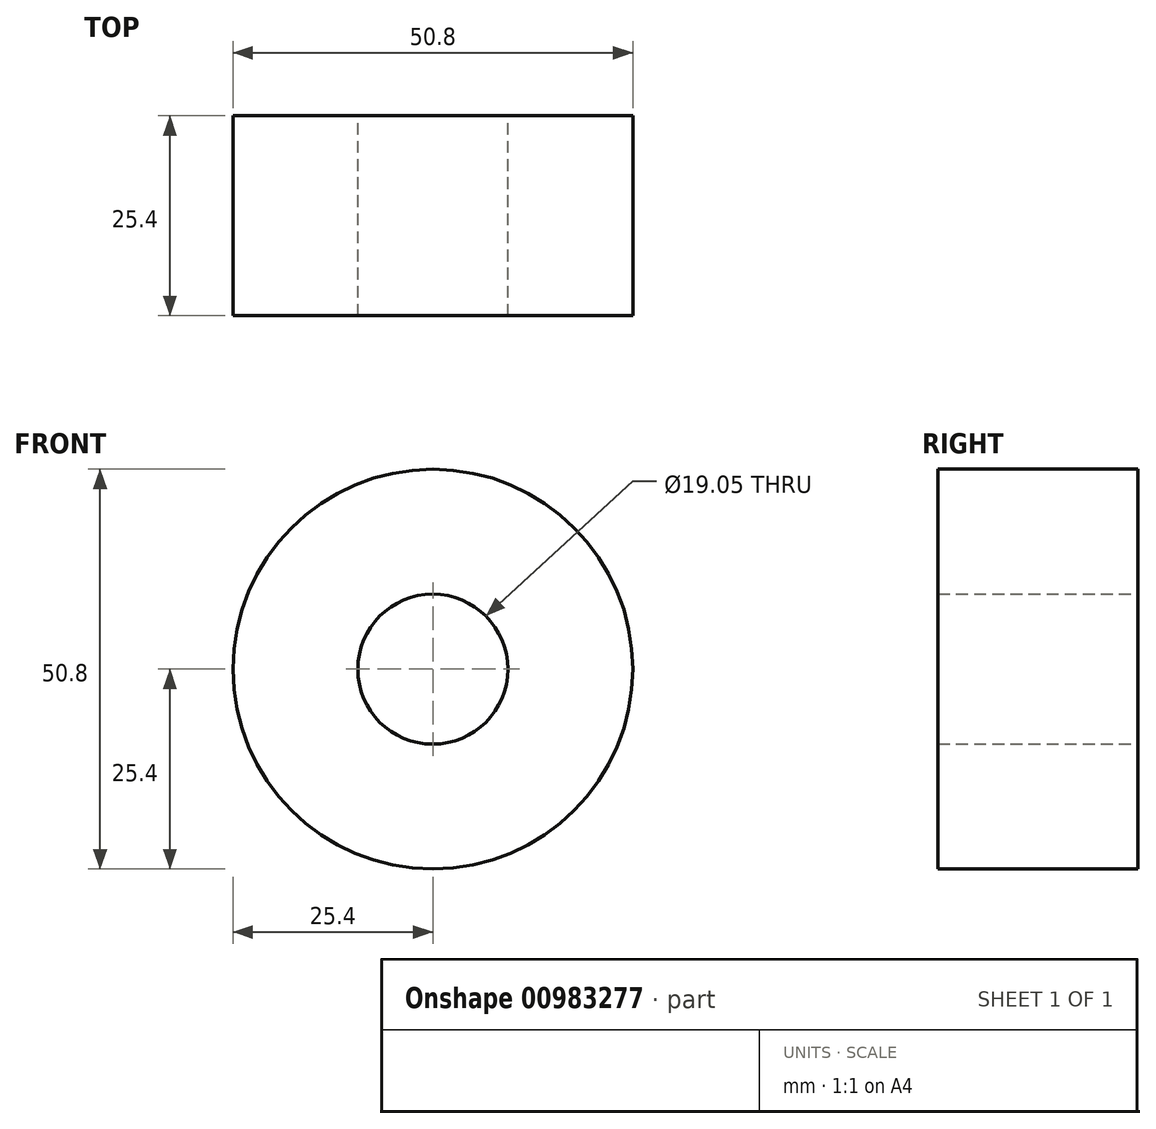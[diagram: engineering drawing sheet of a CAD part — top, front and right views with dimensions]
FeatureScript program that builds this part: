
annotation { "Feature Type Name" : "Feature", "Feature Type Description" : "" }
export const myFeature = defineFeature(function(context is Context, id is Id, definition is map)
    precondition{}
    {
        {
            var Q0;
            Q0=qCreatedBy(makeId("Front.planeOp"),FACE);
            var sketch = newSketch(context, id + "F0", { "sketchPlane" : qUnion([Q0])});
            skCircle(sketch, "E0", {"center": v(0, 0) * mm, "radius": 25.4 * mm});
            skCircle(sketch, "E1", {"center": v(0, 0) * mm, "radius": 9.53 * mm});
            skSolve(sketch);
        }
        {
            var Q0;
            Q0 = qSketchRegion(id + "F0", true);
            extrude(context, id + "F1", {"entities" : qUnion([Q0]), "depth" : 25.4 * mm, "offsetDistance" : 25.4 * mm});
        }
    });
